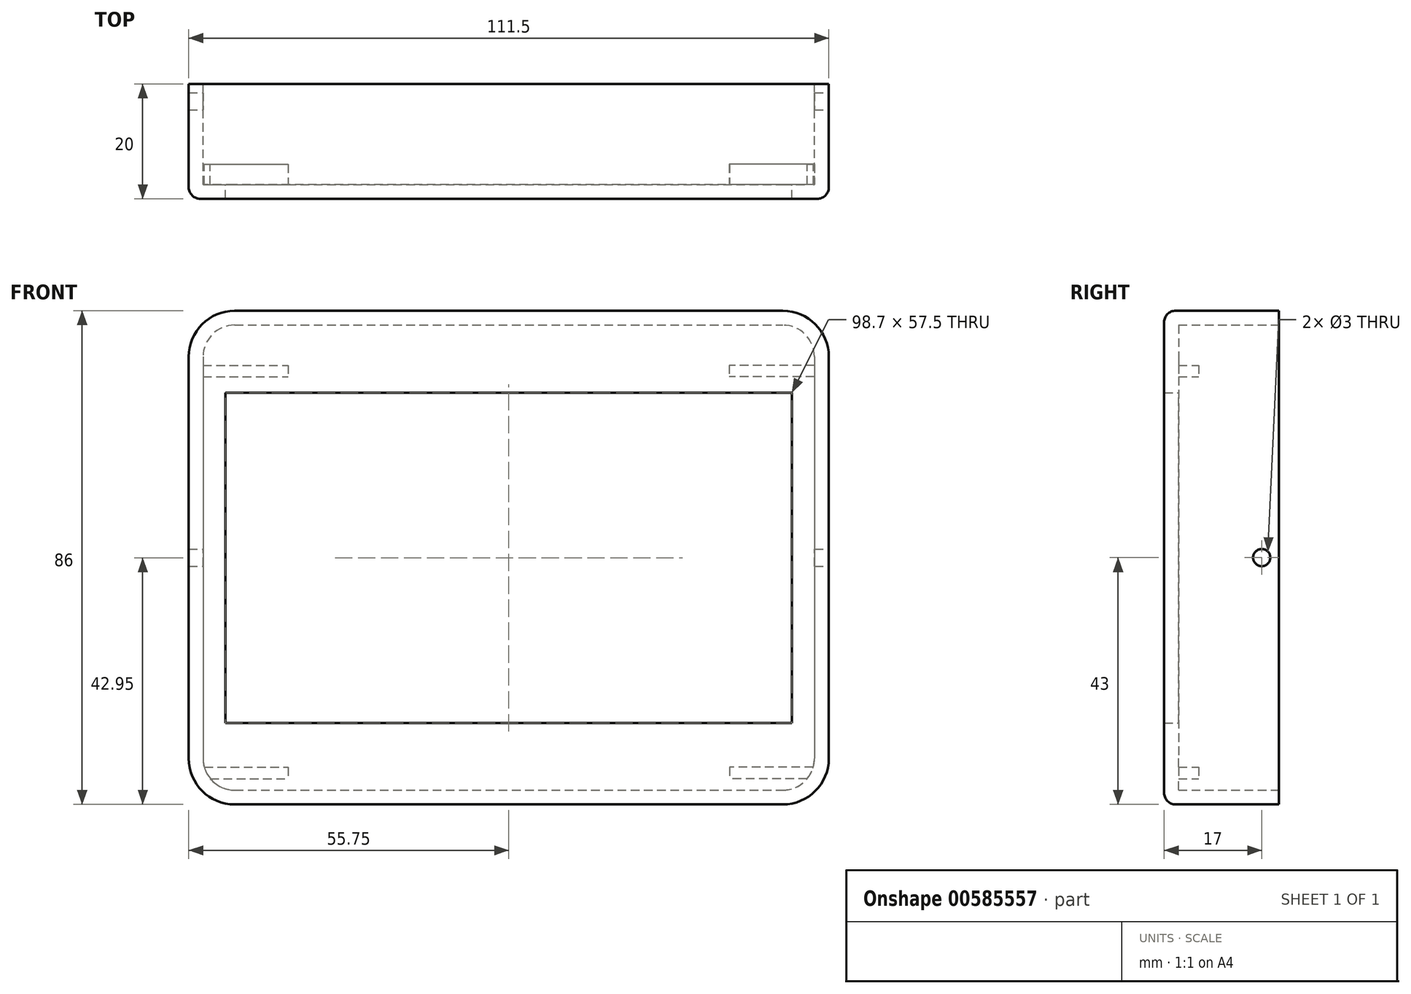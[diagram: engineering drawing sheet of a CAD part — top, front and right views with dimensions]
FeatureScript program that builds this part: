
annotation { "Feature Type Name" : "Feature", "Feature Type Description" : "" }
export const myFeature = defineFeature(function(context is Context, id is Id, definition is map)
    precondition{}
    {
        {
            var Q0;
            Q0=qCreatedBy(makeId("Front.planeOp"),FACE);
            var sketch = newSketch(context, id + "F0", { "sketchPlane" : qUnion([Q0])});
            skLineSegment(sketch, "E0.bottom", {"start": v(-47.75, 43) * mm, "end": v(47.75, 43) * mm});
            skLineSegment(sketch, "E0.top", {"start": v(-47.75, -43) * mm, "end": v(47.75, -43) * mm});
            skLineSegment(sketch, "E0.left", {"start": v(-55.75, 35) * mm, "end": v(-55.75, -35) * mm});
            skLineSegment(sketch, "E0.right", {"start": v(55.75, 35) * mm, "end": v(55.75, -35) * mm});
            skPoint(sketch, "E0.middle", {"position": v(0, 0) * mm});
            skPoint(sketch, "E1.visualSharp", {"position": v(-55.75, 43) * mm});
            skArc(sketch, "E1.filletArc", {"start": v(-47.75, 43) * mm, "mid": v(-53.4, 40.66) * mm, "end": v(-55.75, 35) * mm});
            skPoint(sketch, "E2.visualSharp", {"position": v(55.75, 43) * mm});
            skArc(sketch, "E2.filletArc", {"start": v(55.75, 35) * mm, "mid": v(53.4, 40.66) * mm, "end": v(47.75, 43) * mm});
            skPoint(sketch, "E3.visualSharp", {"position": v(55.75, -43) * mm});
            skArc(sketch, "E3.filletArc", {"start": v(47.75, -43) * mm, "mid": v(53.4, -40.66) * mm, "end": v(55.75, -35) * mm});
            skPoint(sketch, "E4.visualSharp", {"position": v(-55.75, -43) * mm});
            skArc(sketch, "E4.filletArc", {"start": v(-55.75, -35) * mm, "mid": v(-53.4, -40.66) * mm, "end": v(-47.75, -43) * mm});
            skSolve(sketch);
        }
        {
            var Q0;
            Q0=qSketchRegion(id+"F0",true);
            extrude(context, id + "F1", {"entities" : qUnion([Q0]), "depth" : 20 * mm, "offsetDistance" : 25 * mm});
        }
        {
            var Q0;
            Q0=makeQuery(id+"F1.opExtrude","CAP_FACE",FACE,{"disambiguationData":[OSD([sQuery(id+"F0.wireOp",EDGE,"E0.bottom"),sQuery(id+"F0.wireOp",EDGE,"E0.top"),sQuery(id+"F0.wireOp",EDGE,"E0.left"),sQuery(id+"F0.wireOp",EDGE,"E0.right"),sQuery(id+"F0.wireOp",EDGE,"E1.filletArc"),sQuery(id+"F0.wireOp",EDGE,"E2.filletArc"),sQuery(id+"F0.wireOp",EDGE,"E3.filletArc"),sQuery(id+"F0.wireOp",EDGE,"E4.filletArc")])],"isStart":true});
            shell(context, id + "F2", {"entities" : qUnion([Q0]), "thickness" : 2.5 * mm});
        }
        {
            var Q0;
            Q0=qCreatedBy(makeId("Front.planeOp"),FACE);
            cPlane(context, id + "F3", {"entities" : qUnion([Q0]), "cplaneType" : CPlaneType.OFFSET, "offset" : 20 * mm, "width" : 150 * mm, "height" : 150 * mm});
        }
        {
            var Q0;
            Q0=qCreatedBy(id+"F3.planeOp",FACE);
            var sketch = newSketch(context, id + "F4", { "sketchPlane" : qUnion([Q0])});
            skLineSegment(sketch, "E5.bottom", {"start": v(-52.75, 31) * mm, "end": v(52.75, 31) * mm});
            skLineSegment(sketch, "E5.top", {"start": v(-52.75, -36.2) * mm, "end": v(52.75, -36.2) * mm});
            skLineSegment(sketch, "E5.left", {"start": v(-52.75, 31) * mm, "end": v(-52.75, -36.2) * mm});
            skLineSegment(sketch, "E5.right", {"start": v(52.75, 31) * mm, "end": v(52.75, -36.2) * mm});
            skLineSegment(sketch, "E6.bottom", {"start": v(3.16, 40.44) * mm, "end": v(-5.87, 40.44) * mm});
            skLineSegment(sketch, "E6.top", {"start": v(3.16, 31) * mm, "end": v(-5.87, 31) * mm});
            skLineSegment(sketch, "E6.left", {"start": v(3.16, 40.44) * mm, "end": v(3.16, 31) * mm});
            skLineSegment(sketch, "E6.right", {"start": v(-5.87, 40.44) * mm, "end": v(-5.87, 31) * mm});
            skLineSegment(sketch, "E7.bottom", {"start": v(20.63, -36.2) * mm, "end": v(16.48, -36.2) * mm});
            skLineSegment(sketch, "E7.top", {"start": v(20.63, -40.22) * mm, "end": v(16.48, -40.22) * mm});
            skLineSegment(sketch, "E7.left", {"start": v(20.63, -36.2) * mm, "end": v(20.63, -40.22) * mm});
            skLineSegment(sketch, "E7.right", {"start": v(16.48, -36.2) * mm, "end": v(16.48, -40.22) * mm});
            skSolve(sketch);
        }
        {
            var Q0;
            Q0=qCreatedBy(makeId("Front.planeOp"),FACE);
            var sketch = newSketch(context, id + "F5", { "sketchPlane" : qUnion([Q0])});
            skLineSegment(sketch, "E8.bottom", {"start": v(-49.35, 28.7) * mm, "end": v(49.35, 28.7) * mm});
            skLineSegment(sketch, "E8.top", {"start": v(-49.35, -28.8) * mm, "end": v(49.35, -28.8) * mm});
            skLineSegment(sketch, "E8.left", {"start": v(-49.35, 28.7) * mm, "end": v(-49.35, -28.8) * mm});
            skLineSegment(sketch, "E8.right", {"start": v(49.35, 28.7) * mm, "end": v(49.35, -28.8) * mm});
            skSolve(sketch);
        }
        {
            var Q0;
            Q0=makeQuery(id+"F5.imprint","IMPRINT",FACE,{"disambiguationData":[TD([[makeQuery(id+"F5.imprint","IMPRINT",EDGE,{"derivedFrom":sQuery(id+"F5.wireOp",EDGE,"E8.bottom")}),-1.0]])]});
            extrude(context, id + "F6", {"entities" : qUnion([Q0]), "operationType" : NewBodyOperationType.REMOVE, "depth" : 50 * mm});
        }
        {
            var Q0;
            Q0=qCreatedBy(id+"F3.planeOp",FACE);
            var sketch = newSketch(context, id + "F7", { "sketchPlane" : qUnion([Q0])});
            skLineSegment(sketch, "E9.bottom", {"start": v(53.44, -36.5) * mm, "end": v(38.44, -36.5) * mm});
            skLineSegment(sketch, "E9.top", {"start": v(53.44, -38.5) * mm, "end": v(38.44, -38.5) * mm});
            skLineSegment(sketch, "E9.left", {"start": v(53.44, -36.5) * mm, "end": v(53.44, -38.5) * mm});
            skLineSegment(sketch, "E9.right", {"start": v(38.44, -36.5) * mm, "end": v(38.44, -38.5) * mm});
            skLineSegment(sketch, "E10.MirrorCS", {"start": v(-53.44, -36.5) * mm, "end": v(-38.44, -36.5) * mm});
            skLineSegment(sketch, "E11.MirrorCS", {"start": v(-53.44, -36.5) * mm, "end": v(-53.44, -38.5) * mm});
            skLineSegment(sketch, "E12.MirrorCS", {"start": v(-53.44, -38.5) * mm, "end": v(-38.44, -38.5) * mm});
            skLineSegment(sketch, "E13.MirrorCS", {"start": v(-38.44, -36.5) * mm, "end": v(-38.44, -38.5) * mm});
            skLineSegment(sketch, "E14.MirrorCS", {"start": v(-53.44, -29.47) * mm, "end": v(-53.44, -38.5) * mm});
            skLineSegment(sketch, "E15.bottom", {"start": v(53.4, 33.5) * mm, "end": v(38.4, 33.5) * mm});
            skLineSegment(sketch, "E15.top", {"start": v(53.4, 31.5) * mm, "end": v(38.4, 31.5) * mm});
            skLineSegment(sketch, "E15.left", {"start": v(53.4, 33.5) * mm, "end": v(53.4, 31.5) * mm});
            skLineSegment(sketch, "E15.right", {"start": v(38.4, 33.5) * mm, "end": v(38.4, 31.5) * mm});
            skLineSegment(sketch, "E16.MirrorCS", {"start": v(-53.4, 33.5) * mm, "end": v(-38.4, 33.5) * mm});
            skLineSegment(sketch, "E17.MirrorCS", {"start": v(-38.4, 33.5) * mm, "end": v(-38.4, 31.5) * mm});
            skLineSegment(sketch, "E18.MirrorCS", {"start": v(-53.4, 31.5) * mm, "end": v(-38.4, 31.5) * mm});
            skLineSegment(sketch, "E19.MirrorCS", {"start": v(-53.4, 33.5) * mm, "end": v(-53.4, 31.5) * mm});
            skSolve(sketch);
        }
        {
            var Q0;
            Q0=qSketchRegion(id+"F7",true);
            extrude(context, id + "F8", {"entities" : qUnion([Q0]), "operationType" : NewBodyOperationType.ADD, "oppositeDirection" : true, "depth" : 6 * mm, "offsetDistance" : 25 * mm});
        }
        {
            var Q0;
            Q0=qCreatedBy(makeId("Front.planeOp"),FACE);
            cPlane(context, id + "F9", {"entities" : qUnion([Q0]), "cplaneType" : CPlaneType.OFFSET, "offset" : 15 * mm, "width" : 150 * mm, "height" : 150 * mm});
        }
        {
            var Q0;
            Q0=qCreatedBy(makeId("Front.planeOp"),FACE);
            var sketch = newSketch(context, id + "F10", { "sketchPlane" : qUnion([Q0])});
            skLineSegment(sketch, "E20", {"start": v(-67.43, 0) * mm, "end": v(64.52, 0) * mm});
            skSolve(sketch);
        }
        {
            var Q0;
            Q0=makeQuery(id+"F1.opExtrude","CAP_EDGE",EDGE,{"disambiguationData":[OSD([sQuery(id+"F0.wireOp",EDGE,"E0.bottom")])],"isStart":false});
            var Q1;
            Q1=makeQuery(id+"F1.opExtrude","CAP_EDGE",EDGE,{"disambiguationData":[OSD([sQuery(id+"F0.wireOp",EDGE,"E0.right")])],"isStart":false});
            fillet(context, id + "F11", {"entities" : qUnion([Q0, Q1]), "radius" : 2 * mm, "tangentPropagation" : true, "allowEdgeOverflow" : false});
        }
        {
            var Q0;
            Q0=qCreatedBy(makeId("Right.planeOp"),FACE);
            var sketch = newSketch(context, id + "F12", { "sketchPlane" : qUnion([Q0])});
            skCircle(sketch, "E21", {"center": v(-3, 0) * mm, "radius": 1.5 * mm});
            skSolve(sketch);
        }
        {
            var Q0;
            Q0=qSketchRegion(id+"F12",true);
            extrude(context, id + "F13", {"entities" : qUnion([Q0]), "operationType" : NewBodyOperationType.REMOVE, "endBound" : BoundingType.SYMMETRIC, "oppositeDirection" : true, "depth" : 140 * mm, "offsetDistance" : 25 * mm});
        }
    });
